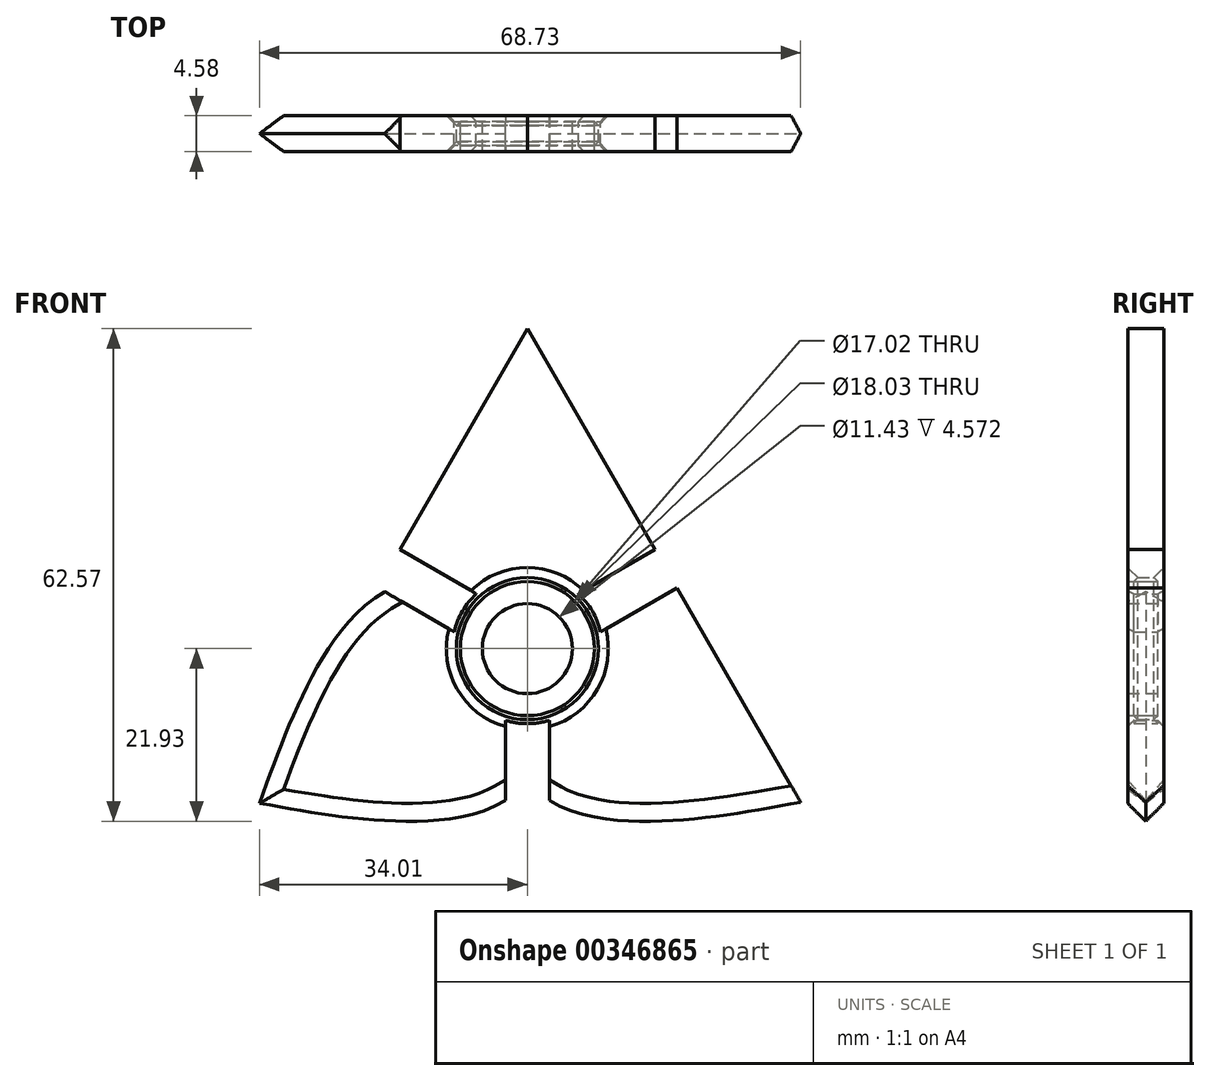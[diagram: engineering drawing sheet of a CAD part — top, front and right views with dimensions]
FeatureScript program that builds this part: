
annotation { "Feature Type Name" : "Feature", "Feature Type Description" : "" }
export const myFeature = defineFeature(function(context is Context, id is Id, definition is map)
    precondition{}
    {
        {
            var Q0;
            Q0=qCreatedBy(makeId("Front.planeOp"),FACE);
            var sketch = newSketch(context, id + "F0", { "sketchPlane" : qUnion([Q0])});
            skArc(sketch, "E0.cCircle", {"start": v(0, -20.32) * mm, "mid": v(16.86, -11.35) * mm, "end": v(18.83, 7.64) * mm, "construction": true});
            skLineSegment(sketch, "E0.0", {"start": v(35.2, -20.32) * mm, "end": v(2.8, -20.32) * mm});
            skLineSegment(sketch, "E0.2", {"start": v(0, 40.64) * mm, "end": v(16.2, 12.58) * mm});
            skLineSegment(sketch, "E1", {"start": v(0, 0) * mm, "end": v(8.25, 4.76) * mm});
            skLineSegment(sketch, "E2", {"start": v(35.2, -20.32) * mm, "end": v(0, 0) * mm});
            skLineSegment(sketch, "E3", {"start": v(0, 40.64) * mm, "end": v(0, -9.52) * mm});
            skArc(sketch, "E4", {"start": v(0, -9.53) * mm, "mid": v(9.53, 0) * mm, "end": v(0, 9.53) * mm});
            skLineSegment(sketch, "E5", {"start": v(16.2, 12.58) * mm, "end": v(6.49, 6.97) * mm});
            skLineSegment(sketch, "E6", {"start": v(19, 7.74) * mm, "end": v(9.28, 2.13) * mm});
            skLineSegment(sketch, "E7", {"start": v(2.8, -20.32) * mm, "end": v(2.8, -9.1) * mm});
            skLineSegment(sketch, "E8", {"start": v(16.2, 12.58) * mm, "end": v(0, 40.64) * mm});
            skLineSegment(sketch, "E9", {"start": v(19, 7.74) * mm, "end": v(35.2, -20.32) * mm});
            skArc(sketch, "E10.trimOffspring", {"start": v(16.03, 12.48) * mm, "mid": v(8.92, 18.26) * mm, "end": v(0, 20.32) * mm, "construction": true});
            skFitSpline(sketch, "E11", {"points": [v(0, 40.64) * mm, v(16.2, 12.58) * mm], "startDerivative": vector(20.94, -24.51) * mm, "endDerivative": vector(0.35, -27.5) * mm});
            skFitSpline(sketch, "E12.MirrorCS", {"points": [v(35.2, -20.32) * mm, v(19, 7.74) * mm], "startDerivative": vector(-10.76, 30.39) * mm, "endDerivative": vector(-23.64, 14.06) * mm});
            skLineSegment(sketch, "E13.MirrorCS", {"start": v(0, 40.64) * mm, "end": v(0, 0) * mm});
            skFitSpline(sketch, "E14.MirrorCS", {"points": [v(35.2, -20.32) * mm, v(2.8, -20.32) * mm], "startDerivative": vector(-31.7, -5.88) * mm, "endDerivative": vector(-24, 13.45) * mm});
            skFitSpline(sketch, "E15.MirrorCS", {"points": [v(0, 40.64) * mm, v(-16.2, 12.58) * mm], "startDerivative": vector(-20.94, -24.51) * mm, "endDerivative": vector(-0.35, -27.5) * mm});
            skLineSegment(sketch, "E16.MirrorCS", {"start": v(0, 40.64) * mm, "end": v(-16.2, 12.58) * mm});
            skLineSegment(sketch, "E17.MirrorCS", {"start": v(-19, 7.74) * mm, "end": v(-35.2, -20.32) * mm});
            skArc(sketch, "E18.MirrorCS", {"start": v(-16.03, 12.48) * mm, "mid": v(-8.92, 18.26) * mm, "end": v(0, 20.32) * mm, "construction": true});
            skFitSpline(sketch, "E19.MirrorCS", {"points": [v(-35.2, -20.32) * mm, v(-19, 7.74) * mm], "startDerivative": vector(10.76, 30.39) * mm, "endDerivative": vector(23.64, 14.06) * mm});
            skArc(sketch, "E20.MirrorCS", {"start": v(0, -20.32) * mm, "mid": v(-16.86, -11.35) * mm, "end": v(-18.83, 7.64) * mm, "construction": true});
            skLineSegment(sketch, "E21.MirrorCS", {"start": v(-35.2, -20.32) * mm, "end": v(-2.8, -20.32) * mm});
            skFitSpline(sketch, "E22.MirrorCS", {"points": [v(-35.2, -20.32) * mm, v(-2.8, -20.32) * mm], "startDerivative": vector(31.7, -5.88) * mm, "endDerivative": vector(24, 13.45) * mm});
            skLineSegment(sketch, "E23.MirrorCS", {"start": v(0, 0) * mm, "end": v(-8.25, 4.76) * mm});
            skLineSegment(sketch, "E24.MirrorCS", {"start": v(-35.2, -20.32) * mm, "end": v(0, 0) * mm});
            skArc(sketch, "E25.MirrorCS", {"start": v(0, -9.53) * mm, "mid": v(-9.53, 0) * mm, "end": v(0, 9.53) * mm});
            skLineSegment(sketch, "E26.MirrorCS", {"start": v(-16.2, 12.58) * mm, "end": v(-6.49, 6.97) * mm});
            skLineSegment(sketch, "E27.MirrorCS", {"start": v(-19, 7.74) * mm, "end": v(-9.28, 2.13) * mm});
            skLineSegment(sketch, "E28.MirrorCS", {"start": v(-2.8, -20.32) * mm, "end": v(-2.8, -9.1) * mm});
            skLineSegment(sketch, "E29.MirrorCS", {"start": v(-16.2, 12.58) * mm, "end": v(0, 40.64) * mm});
            skArc(sketch, "E30.0", {"start": v(0, -5.72) * mm, "mid": v(5.72, 0) * mm, "end": v(0, 5.72) * mm});
            skArc(sketch, "E31.0", {"start": v(0, -5.72) * mm, "mid": v(-5.72, 0) * mm, "end": v(0, 5.72) * mm});
            skArc(sketch, "E32.0", {"start": v(0, -8.5) * mm, "mid": v(8.5, 0) * mm, "end": v(0, 8.5) * mm});
            skArc(sketch, "E33.0", {"start": v(0, -8.5) * mm, "mid": v(-8.5, 0) * mm, "end": v(0, 8.5) * mm});
            skArc(sketch, "E34.0", {"start": v(0, -9.02) * mm, "mid": v(9.02, 0) * mm, "end": v(0, 9.02) * mm});
            skArc(sketch, "E35.0", {"start": v(0, -9.02) * mm, "mid": v(-9.02, 0) * mm, "end": v(0, 9.02) * mm});
            skSolve(sketch);
        }
        {
            var Q0;
            {var subQ4=sQuery(id+"F0.wireOp",EDGE,"E27.MirrorCS");Q0=makeQuery(id+"F0.imprint","IMPRINT",FACE,{"disambiguationData":[TD([[makeQuery(id+"F0.imprint","IMPRINT",EDGE,{"derivedFrom":subQ4}),-1.0]])]});}
            var Q1;
            {var subQ3=sQuery(id+"F0.wireOp",EDGE,"E26.MirrorCS");Q1=makeQuery(id+"F0.imprint","IMPRINT",FACE,{"disambiguationData":[TD([[makeQuery(id+"F0.imprint","IMPRINT",EDGE,{"derivedFrom":subQ3}),1.0]])]});}
            var Q2;
            Q2=makeQuery(id+"F0.imprint","IMPRINT",FACE,{"disambiguationData":[TD([[makeQuery(id+"F0.imprint","IMPRINT",EDGE,{"derivedFrom":sQuery(id+"F0.wireOp",EDGE,"E0.0")}),1.0]])]});
            var Q3;
            Q3=makeQuery(id+"F0.imprint","IMPRINT",FACE,{"disambiguationData":[TD([[makeQuery(id+"F0.imprint","IMPRINT",EDGE,{"derivedFrom":sQuery(id+"F0.wireOp",EDGE,"E8")}),-1.0]])]});
            var Q4;
            Q4=makeQuery(id+"F0.imprint","IMPRINT",FACE,{"disambiguationData":[TD([[makeQuery(id+"F0.imprint","IMPRINT",EDGE,{"derivedFrom":sQuery(id+"F0.wireOp",EDGE,"E19.MirrorCS")}),-1.0]])]});
            var Q5;
            Q5=makeQuery(id+"F0.imprint","IMPRINT",FACE,{"disambiguationData":[TD([[makeQuery(id+"F0.imprint","IMPRINT",EDGE,{"derivedFrom":sQuery(id+"F0.wireOp",EDGE,"E21.MirrorCS")}),-1.0]])]});
            var Q6;
            Q6=makeQuery(id+"F0.imprint","IMPRINT",FACE,{"disambiguationData":[TD([[makeQuery(id+"F0.imprint","IMPRINT",EDGE,{"derivedFrom":sQuery(id+"F0.wireOp",EDGE,"E29.MirrorCS")}),1.0]])]});
            var Q7;
            {var subQ0=sQuery(id+"F0.wireOp",EDGE,"E0.0");Q7=makeQuery(id+"F0.imprint","IMPRINT",FACE,{"disambiguationData":[TD([[makeQuery(id+"F0.imprint","IMPRINT",EDGE,{"derivedFrom":subQ0}),-1.0]])]});}
            var Q8;
            {var subQ4=sQuery(id+"F0.wireOp",EDGE,"E6");Q8=makeQuery(id+"F0.imprint","IMPRINT",FACE,{"disambiguationData":[TD([[makeQuery(id+"F0.imprint","IMPRINT",EDGE,{"derivedFrom":subQ4}),1.0]])]});}
            var Q9;
            {var subQ3=sQuery(id+"F0.wireOp",EDGE,"E5");Q9=makeQuery(id+"F0.imprint","IMPRINT",FACE,{"disambiguationData":[TD([[makeQuery(id+"F0.imprint","IMPRINT",EDGE,{"derivedFrom":subQ3}),-1.0]])]});}
            var Q10;
            {var subQ0=sQuery(id+"F0.wireOp",EDGE,"E21.MirrorCS");Q10=makeQuery(id+"F0.imprint","IMPRINT",FACE,{"disambiguationData":[TD([[makeQuery(id+"F0.imprint","IMPRINT",EDGE,{"derivedFrom":subQ0}),1.0]])]});}
            var Q11;
            Q11=makeQuery(id+"F0.imprint","IMPRINT",FACE,{"disambiguationData":[TD([[makeQuery(id+"F0.imprint","IMPRINT",EDGE,{"derivedFrom":sQuery(id+"F0.wireOp",EDGE,"E9")}),1.0]])]});
            var Q12;
            {var subQ0=sQuery(id+"F0.wireOp",EDGE,"E25.MirrorCS");var subQ6=sQuery(id+"F0.wireOp",EDGE,"E24.MirrorCS");var subQ7=makeQuery(id+"F0.imprint","INTERSECT",VERTEX,{"derivedFrom":[subQ6,subQ0]});Q12=makeQuery(id+"F0.imprint","IMPRINT",FACE,{"disambiguationData":[TD([[makeQuery(id+"F0.imprint","IMPRINT",EDGE,{"disambiguationData":[TD([[subQ7,-1.0]])],"derivedFrom":subQ6}),-1.0]])]});}
            var Q13;
            {var subQ0=sQuery(id+"F0.wireOp",EDGE,"E25.MirrorCS");var subQ1=sQuery(id+"F0.wireOp",EDGE,"E23.MirrorCS");var subQ2=makeQuery(id+"F0.imprint","INTERSECT",VERTEX,{"derivedFrom":[subQ1,subQ0]});Q13=makeQuery(id+"F0.imprint","IMPRINT",FACE,{"disambiguationData":[TD([[makeQuery(id+"F0.imprint","IMPRINT",EDGE,{"disambiguationData":[TD([[subQ2,1.0]])],"derivedFrom":subQ1}),1.0]])]});}
            var Q14;
            {var subQ1=sQuery(id+"F0.wireOp",EDGE,"E25.MirrorCS");var subQ6=sQuery(id+"F0.wireOp",EDGE,"E23.MirrorCS");var subQ7=makeQuery(id+"F0.imprint","INTERSECT",VERTEX,{"derivedFrom":[subQ6,subQ1]});Q14=makeQuery(id+"F0.imprint","IMPRINT",FACE,{"disambiguationData":[TD([[makeQuery(id+"F0.imprint","IMPRINT",EDGE,{"disambiguationData":[TD([[subQ7,1.0]])],"derivedFrom":subQ6}),-1.0]])]});}
            var Q15;
            {var subQ1=sQuery(id+"F0.wireOp",EDGE,"E4");var subQ6=sQuery(id+"F0.wireOp",EDGE,"E1");var subQ7=makeQuery(id+"F0.imprint","INTERSECT",VERTEX,{"derivedFrom":[subQ6,subQ1]});Q15=makeQuery(id+"F0.imprint","IMPRINT",FACE,{"disambiguationData":[TD([[makeQuery(id+"F0.imprint","IMPRINT",EDGE,{"disambiguationData":[TD([[subQ7,1.0]])],"derivedFrom":subQ6}),1.0]])]});}
            var Q16;
            {var subQ0=sQuery(id+"F0.wireOp",EDGE,"E4");var subQ4=sQuery(id+"F0.wireOp",EDGE,"E1");var subQ5=makeQuery(id+"F0.imprint","INTERSECT",VERTEX,{"derivedFrom":[subQ4,subQ0]});Q16=makeQuery(id+"F0.imprint","IMPRINT",FACE,{"disambiguationData":[TD([[makeQuery(id+"F0.imprint","IMPRINT",EDGE,{"disambiguationData":[TD([[subQ5,1.0]])],"derivedFrom":subQ4}),-1.0]])]});}
            var Q17;
            {var subQ0=sQuery(id+"F0.wireOp",EDGE,"E4");var subQ2=sQuery(id+"F0.wireOp",EDGE,"E2");var subQ3=makeQuery(id+"F0.imprint","INTERSECT",VERTEX,{"derivedFrom":[subQ2,subQ0]});Q17=makeQuery(id+"F0.imprint","IMPRINT",FACE,{"disambiguationData":[TD([[makeQuery(id+"F0.imprint","IMPRINT",EDGE,{"disambiguationData":[TD([[subQ3,-1.0]])],"derivedFrom":subQ2}),1.0]])]});}
            var Q18;
            {var subQ0=sQuery(id+"F0.wireOp",EDGE,"E30.0");var subQ1=sQuery(id+"F0.wireOp",EDGE,"E1");var subQ2=makeQuery(id+"F0.imprint","INTERSECT",VERTEX,{"derivedFrom":[subQ1,subQ0]});Q18=makeQuery(id+"F0.imprint","IMPRINT",FACE,{"disambiguationData":[TD([[makeQuery(id+"F0.imprint","IMPRINT",EDGE,{"disambiguationData":[TD([[subQ2,-1.0]])],"derivedFrom":subQ1}),-1.0]])]});}
            var Q19;
            {var subQ0=sQuery(id+"F0.wireOp",EDGE,"E30.0");var subQ1=sQuery(id+"F0.wireOp",EDGE,"E1");var subQ2=makeQuery(id+"F0.imprint","INTERSECT",VERTEX,{"derivedFrom":[subQ1,subQ0]});Q19=makeQuery(id+"F0.imprint","IMPRINT",FACE,{"disambiguationData":[TD([[makeQuery(id+"F0.imprint","IMPRINT",EDGE,{"disambiguationData":[TD([[subQ2,-1.0]])],"derivedFrom":subQ1}),1.0]])]});}
            var Q20;
            {var subQ0=sQuery(id+"F0.wireOp",EDGE,"E31.0");var subQ1=sQuery(id+"F0.wireOp",EDGE,"E23.MirrorCS");var subQ2=makeQuery(id+"F0.imprint","INTERSECT",VERTEX,{"derivedFrom":[subQ1,subQ0]});Q20=makeQuery(id+"F0.imprint","IMPRINT",FACE,{"disambiguationData":[TD([[makeQuery(id+"F0.imprint","IMPRINT",EDGE,{"disambiguationData":[TD([[subQ2,-1.0]])],"derivedFrom":subQ1}),-1.0]])]});}
            var Q21;
            {var subQ0=sQuery(id+"F0.wireOp",EDGE,"E31.0");var subQ1=sQuery(id+"F0.wireOp",EDGE,"E23.MirrorCS");var subQ2=makeQuery(id+"F0.imprint","INTERSECT",VERTEX,{"derivedFrom":[subQ1,subQ0]});Q21=makeQuery(id+"F0.imprint","IMPRINT",FACE,{"disambiguationData":[TD([[makeQuery(id+"F0.imprint","IMPRINT",EDGE,{"disambiguationData":[TD([[subQ2,-1.0]])],"derivedFrom":subQ1}),1.0]])]});}
            var Q22;
            {var subQ0=sQuery(id+"F0.wireOp",EDGE,"E33.0");var subQ1=sQuery(id+"F0.wireOp",EDGE,"E24.MirrorCS");var subQ2=makeQuery(id+"F0.imprint","INTERSECT",VERTEX,{"derivedFrom":[subQ1,subQ0]});Q22=makeQuery(id+"F0.imprint","IMPRINT",FACE,{"disambiguationData":[TD([[makeQuery(id+"F0.imprint","IMPRINT",EDGE,{"disambiguationData":[TD([[subQ2,-1.0]])],"derivedFrom":subQ1}),-1.0]])]});}
            var Q23;
            {var subQ0=sQuery(id+"F0.wireOp",EDGE,"E32.0");var subQ1=sQuery(id+"F0.wireOp",EDGE,"E2");var subQ2=makeQuery(id+"F0.imprint","INTERSECT",VERTEX,{"derivedFrom":[subQ1,subQ0]});Q23=makeQuery(id+"F0.imprint","IMPRINT",FACE,{"disambiguationData":[TD([[makeQuery(id+"F0.imprint","IMPRINT",EDGE,{"disambiguationData":[TD([[subQ2,-1.0]])],"derivedFrom":subQ1}),1.0]])]});}
            extrude(context, id + "F1", {"entities" : qUnion([Q0, Q1, Q2, Q3, Q4, Q5, Q6, Q7, Q8, Q9, Q10, Q11, Q12, Q13, Q14, Q15, Q16, Q17, Q18, Q19, Q20, Q21, Q22, Q23]), "endBound" : BoundingType.SYMMETRIC, "depth" : 4.57 * mm});
        }
        {
            var Q0;
            Q0=makeQuery(id+"F1.opExtrude","CAP_EDGE",EDGE,{"disambiguationData":[OSD([sQuery(id+"F0.wireOp",EDGE,"E14.MirrorCS")])],"isStart":false});
            var Q1;
            Q1=makeQuery(id+"F1.opExtrude","CAP_EDGE",EDGE,{"disambiguationData":[OSD([sQuery(id+"F0.wireOp",EDGE,"E12.MirrorCS")])],"isStart":false});
            var Q2;
            Q2=makeQuery(id+"F1.opExtrude","CAP_EDGE",EDGE,{"disambiguationData":[OSD([sQuery(id+"F0.wireOp",EDGE,"E11")])],"isStart":false});
            var Q3;
            Q3=makeQuery(id+"F1.opExtrude","CAP_EDGE",EDGE,{"disambiguationData":[OSD([sQuery(id+"F0.wireOp",EDGE,"E15.MirrorCS")])],"isStart":false});
            var Q4;
            Q4=makeQuery(id+"F1.opExtrude","CAP_EDGE",EDGE,{"disambiguationData":[OSD([sQuery(id+"F0.wireOp",EDGE,"E19.MirrorCS")])],"isStart":false});
            var Q5;
            Q5=makeQuery(id+"F1.opExtrude","CAP_EDGE",EDGE,{"disambiguationData":[OSD([sQuery(id+"F0.wireOp",EDGE,"E22.MirrorCS")])],"isStart":false});
            var Q6;
            Q6=makeQuery(id+"F1.opExtrude","CAP_EDGE",EDGE,{"disambiguationData":[OSD([sQuery(id+"F0.wireOp",EDGE,"E14.MirrorCS")])],"isStart":true});
            var Q7;
            Q7=makeQuery(id+"F1.opExtrude","CAP_EDGE",EDGE,{"disambiguationData":[OSD([sQuery(id+"F0.wireOp",EDGE,"E12.MirrorCS")])],"isStart":true});
            var Q8;
            Q8=makeQuery(id+"F1.opExtrude","CAP_EDGE",EDGE,{"disambiguationData":[OSD([sQuery(id+"F0.wireOp",EDGE,"E11")])],"isStart":true});
            var Q9;
            Q9=makeQuery(id+"F1.opExtrude","CAP_EDGE",EDGE,{"disambiguationData":[OSD([sQuery(id+"F0.wireOp",EDGE,"E15.MirrorCS")])],"isStart":true});
            var Q10;
            Q10=makeQuery(id+"F1.opExtrude","CAP_EDGE",EDGE,{"disambiguationData":[OSD([sQuery(id+"F0.wireOp",EDGE,"E19.MirrorCS")])],"isStart":true});
            var Q11;
            Q11=makeQuery(id+"F1.opExtrude","CAP_EDGE",EDGE,{"disambiguationData":[OSD([sQuery(id+"F0.wireOp",EDGE,"E22.MirrorCS")])],"isStart":true});
            chamfer(context, id + "F2", {"entities" : qUnion([Q0, Q1, Q2, Q3, Q4, Q5, Q6, Q7, Q8, Q9, Q10, Q11]), "width" : 3.17 * mm, "tangentPropagation" : true});
        }
        {
            var Q0;
            {var subQ0=sQuery(id+"F0.wireOp",EDGE,"E32.0");var subQ1=sQuery(id+"F0.wireOp",EDGE,"E1");var subQ2=makeQuery(id+"F0.imprint","INTERSECT",VERTEX,{"derivedFrom":[subQ1,subQ0]});Q0=makeQuery(id+"F0.imprint","IMPRINT",FACE,{"disambiguationData":[TD([[makeQuery(id+"F0.imprint","IMPRINT",EDGE,{"disambiguationData":[TD([[subQ2,-1.0]])],"derivedFrom":subQ1}),-1.0]])]});}
            var Q1;
            {var subQ0=sQuery(id+"F0.wireOp",EDGE,"E32.0");var subQ1=sQuery(id+"F0.wireOp",EDGE,"E1");var subQ2=makeQuery(id+"F0.imprint","INTERSECT",VERTEX,{"derivedFrom":[subQ1,subQ0]});Q1=makeQuery(id+"F0.imprint","IMPRINT",FACE,{"disambiguationData":[TD([[makeQuery(id+"F0.imprint","IMPRINT",EDGE,{"disambiguationData":[TD([[subQ2,-1.0]])],"derivedFrom":subQ1}),1.0]])]});}
            var Q2;
            {var subQ0=sQuery(id+"F0.wireOp",EDGE,"E34.0");var subQ1=sQuery(id+"F0.wireOp",EDGE,"E2");var subQ2=makeQuery(id+"F0.imprint","INTERSECT",VERTEX,{"derivedFrom":[subQ1,subQ0]});Q2=makeQuery(id+"F0.imprint","IMPRINT",FACE,{"disambiguationData":[TD([[makeQuery(id+"F0.imprint","IMPRINT",EDGE,{"disambiguationData":[TD([[subQ2,-1.0]])],"derivedFrom":subQ1}),1.0]])]});}
            var Q3;
            {var subQ0=sQuery(id+"F0.wireOp",EDGE,"E35.0");var subQ1=sQuery(id+"F0.wireOp",EDGE,"E24.MirrorCS");var subQ2=makeQuery(id+"F0.imprint","INTERSECT",VERTEX,{"derivedFrom":[subQ1,subQ0]});Q3=makeQuery(id+"F0.imprint","IMPRINT",FACE,{"disambiguationData":[TD([[makeQuery(id+"F0.imprint","IMPRINT",EDGE,{"disambiguationData":[TD([[subQ2,-1.0]])],"derivedFrom":subQ1}),-1.0]])]});}
            var Q4;
            {var subQ0=sQuery(id+"F0.wireOp",EDGE,"E33.0");var subQ1=sQuery(id+"F0.wireOp",EDGE,"E23.MirrorCS");var subQ2=makeQuery(id+"F0.imprint","INTERSECT",VERTEX,{"derivedFrom":[subQ1,subQ0]});Q4=makeQuery(id+"F0.imprint","IMPRINT",FACE,{"disambiguationData":[TD([[makeQuery(id+"F0.imprint","IMPRINT",EDGE,{"disambiguationData":[TD([[subQ2,-1.0]])],"derivedFrom":subQ1}),-1.0]])]});}
            var Q5;
            {var subQ0=sQuery(id+"F0.wireOp",EDGE,"E33.0");var subQ1=sQuery(id+"F0.wireOp",EDGE,"E23.MirrorCS");var subQ2=makeQuery(id+"F0.imprint","INTERSECT",VERTEX,{"derivedFrom":[subQ1,subQ0]});Q5=makeQuery(id+"F0.imprint","IMPRINT",FACE,{"disambiguationData":[TD([[makeQuery(id+"F0.imprint","IMPRINT",EDGE,{"disambiguationData":[TD([[subQ2,-1.0]])],"derivedFrom":subQ1}),1.0]])]});}
            extrude(context, id + "F3", {"entities" : qUnion([Q0, Q1, Q2, Q3, Q4, Q5]), "endBound" : BoundingType.SYMMETRIC, "depth" : 3.05 * mm});
        }
        {
            var Q0;
            Q0=makeQuery(id+"F1.opExtrude","CAP_EDGE",EDGE,{"disambiguationData":[OSD([sQuery(id+"F0.wireOp",EDGE,"E34.0"),sQuery(id+"F0.wireOp",EDGE,"E35.0")])],"isStart":false});
            chamfer(context, id + "F4", {"entities" : qUnion([Q0]), "width" : 1.27 * mm, "tangentPropagation" : true});
        }
        {
            var Q0;
            Q0=makeQuery(id+"F3.opExtrude","CAP_EDGE",EDGE,{"disambiguationData":[OSD([sQuery(id+"F0.wireOp",EDGE,"E34.0"),sQuery(id+"F0.wireOp",EDGE,"E35.0")])],"isStart":false});
            chamfer(context, id + "F5", {"entities" : qUnion([Q0]), "width" : 0.5 * mm, "tangentPropagation" : true});
        }
        {
            var Q0;
            Q0=makeQuery(id+"F1.opExtrude","CAP_EDGE",EDGE,{"disambiguationData":[OSD([sQuery(id+"F0.wireOp",EDGE,"E34.0"),sQuery(id+"F0.wireOp",EDGE,"E35.0")])],"isStart":true});
            chamfer(context, id + "F6", {"entities" : qUnion([Q0]), "width" : 1.27 * mm, "tangentPropagation" : true});
        }
        {
            var Q0;
            Q0=makeQuery(id+"F3.opExtrude","CAP_EDGE",EDGE,{"disambiguationData":[OSD([sQuery(id+"F0.wireOp",EDGE,"E34.0"),sQuery(id+"F0.wireOp",EDGE,"E35.0")])],"isStart":true});
            chamfer(context, id + "F7", {"entities" : qUnion([Q0]), "width" : 0.5 * mm, "tangentPropagation" : true});
        }
    });
